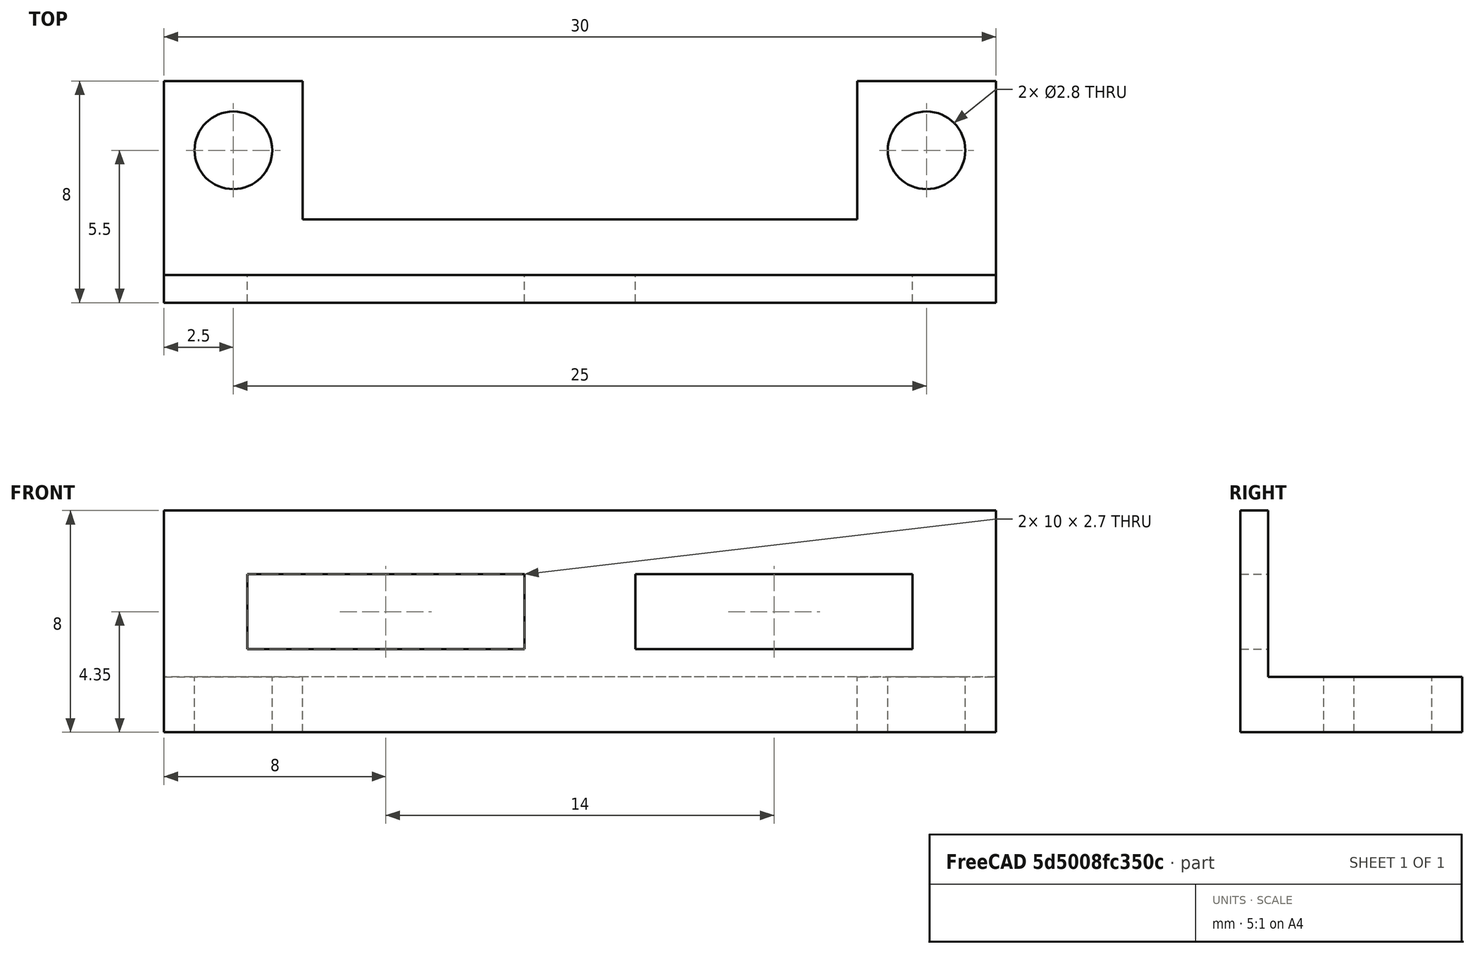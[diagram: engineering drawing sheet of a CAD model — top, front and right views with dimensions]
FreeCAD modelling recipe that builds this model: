
FCSTD DOCUMENT  (FreeCAD 0.15R4671 (Git))
Label: chiphalter_4Löcher_fertisch
License: All rights reserved
LicenseURL: http://en.wikipedia.org/wiki/All_rights_reserved
objects: Part::Box×5, Part::Cut×5, Part::Cylinder×2, Part::MultiFuse×1
note: 13 computed .brp shape members not serialized (recipe doc carries the construction recipe); baked Part::Feature solids carry a one-line shape summary decoded from their .brp

FEATURE [Part::Box] Box  label="Würfel"
  Height = 8
  Length = 30
  Width = 1
FEATURE [Part::Box] Box001  label="Würfel001"
  Height = 2
  Length = 30
  Width = 8
FEATURE [Part::Box] Box002  label="Würfel002"
  Height = 10
  Length = 20
  Placement = pos=(5,3,0) rot=(0,0,1;0rad)
  Width = 5
FEATURE [Part::Cut] Cut
  Base = -> Box001
  Tool = -> Box002
FEATURE [Part::MultiFuse] Fusion
  Shapes = -> [Cut,Box]
FEATURE [Part::Cylinder] Cylinder  label="Zylinder"
  Angle = 360
  Height = 10
  Placement = pos=(2.5,5.5,0) rot=(0,0,1;0rad)
  Radius = 1.4
FEATURE [Part::Cylinder] Cylinder001  label="Zylinder001"
  Angle = 360
  Height = 10
  Placement = pos=(27.5,5.5,0) rot=(0,0,1;0rad)
  Radius = 1.4
FEATURE [Part::Cut] Cut001
  Base = -> Fusion
  Tool = -> Cylinder
FEATURE [Part::Cut] Cut002
  Base = -> Cut001
  Tool = -> Cylinder001
FEATURE [Part::Box] Box003  label="Würfel003"
  Height = 2.7
  Length = 10
  Placement = pos=(17,0,3) rot=(0,0,1;0rad)
  Width = 10
FEATURE [Part::Box] Box004  label="Würfel004"
  Height = 2.7
  Length = 10
  Placement = pos=(3,0,3) rot=(0,0,1;0rad)
  Width = 10
FEATURE [Part::Cut] Cut003
  Base = -> Cut002
  Tool = -> Box004
FEATURE [Part::Cut] Cut004
  Base = -> Cut003
  Tool = -> Box003
